# Revit family: Sink-Wall_Mount-Lavatory-KOHLER-Folio-K-2018IN_1
name_source: partatom
category: Plumbing Fixtures
revit_build: Autodesk Revit 2017 (Build: 20160225_1515(x64)
units: mm (PartAtom-declared; Revit-internal decimal feet)

## family parameters
Cut with Voids When Loaded = No
Host = Face
OmniClass Number = 23.31.13.00
OmniClass Title = Sinks
Part Type = Normal
Room Calculation Point = No
Round Connector Dimension = Use Diameter
Shared = No

## types (2) — shared parameters
ADA Compliant = No
Assembly Code = D2010400
CW Connection = No
Cold Water Inlet = Cold Water Inlet
Date Modified = 06/18/2020
Default Elevation = 36"
Drain Included = No
Finish = Kohler-Vitreous_China-0-White
HW Connection = No
Height = 9 1/4"
Hot Water Inlet = Hot Water Inlet
Length = 24"
Manufacturer = KOHLER Co.
Master Format 2014 = 22 41 16
Master Format 2014 Name = Residential Lavatories and Sinks
Material = Vitreous China
Product Name = Folio
URL = https://www.kohler.co.in
Vent Connection = No
Waste Connection = Yes
Waste Water Outlet = Waste Water Outlet
WaterSense Certified = No
Width = 18 7/8"

## per-type parameters (varying)
| type | Description | Model | Product Documentation Link | Product Page URL | Type |
| 1WH, Single Hole, 0-White | Wall-mount lavatory with single faucet hole | K-2018IN-1WH-0 | http://resources.kohler.com | https://www.kohler.co.in | 1 |
| 1, Single Hole, 0-White | Lavatory with single faucet hole | K-2018IN-1-0 |  |  | 2 |

## geometry (parser evidence)
native form markers: Sweep x6
no freeform markers — native parametric forms only
